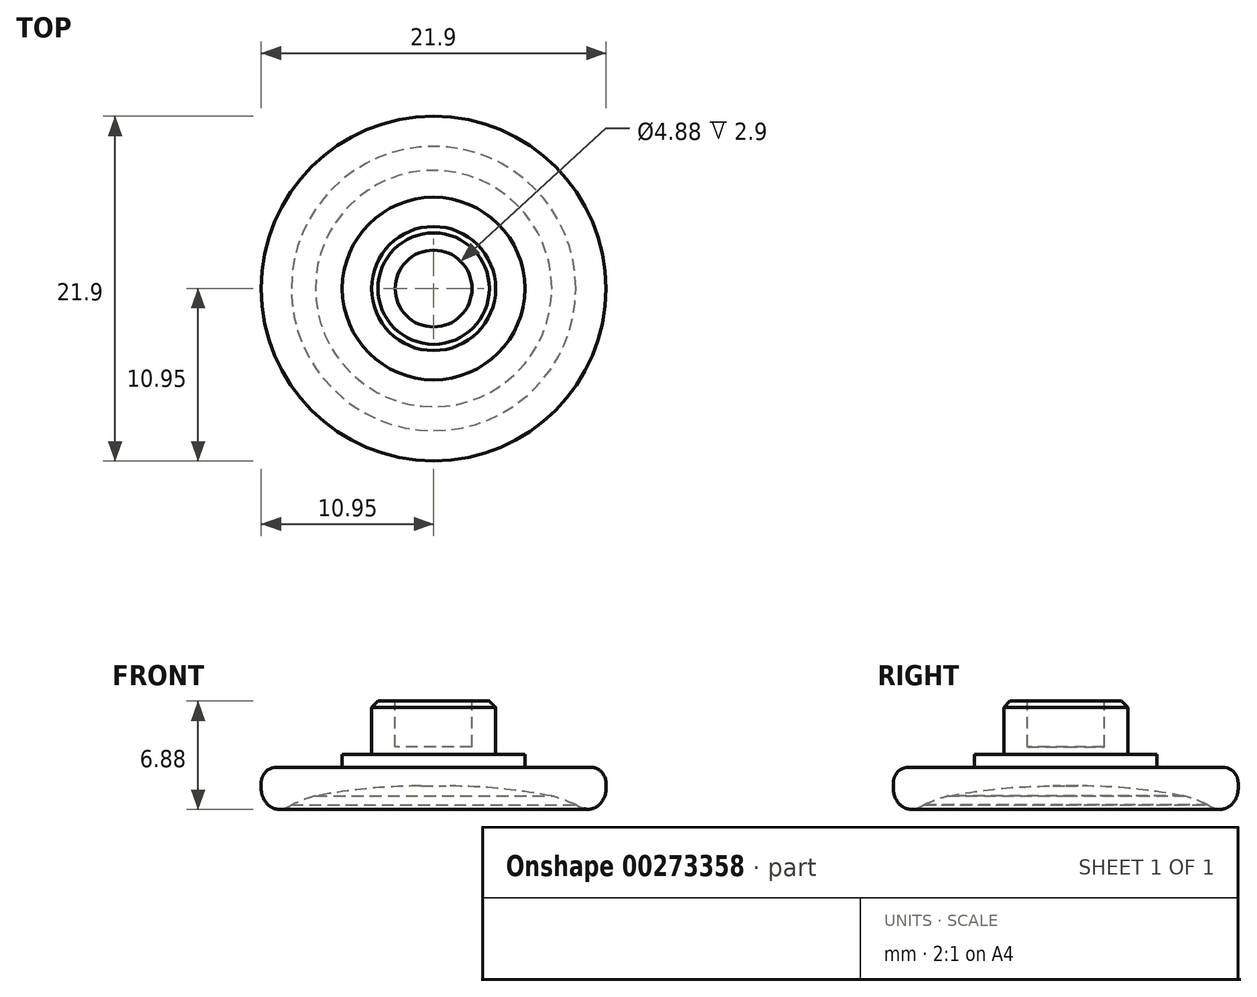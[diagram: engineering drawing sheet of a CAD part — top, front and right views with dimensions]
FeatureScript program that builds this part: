
annotation { "Feature Type Name" : "Feature", "Feature Type Description" : "" }
export const myFeature = defineFeature(function(context is Context, id is Id, definition is map)
    precondition{}
    {
        {
            var Q0;
            Q0=qCreatedBy(makeId("Top.planeOp"),FACE);
            var sketch = newSketch(context, id + "F0", { "sketchPlane" : qUnion([Q0])});
            skCircle(sketch, "E0", {"center": v(0, 0) * mm, "radius": 10.95 * mm});
            skSolve(sketch);
        }
        {
            var Q0;
            Q0=makeQuery(id+"F0.imprint","IMPRINT",FACE,{"disambiguationData":[TD([[makeQuery(id+"F0.imprint","IMPRINT",EDGE,{"derivedFrom":sQuery(id+"F0.wireOp",EDGE,"E0")}),1.0]])]});
            extrude(context, id + "F1", {"entities" : qUnion([Q0]), "depth" : 2.7 * mm});
        }
        {
            var Q0;
            Q0=makeQuery(id+"F1.opExtrude","CAP_FACE",FACE,{"disambiguationData":[OSD([sQuery(id+"F0.wireOp",EDGE,"E0")])],"isStart":false});
            var sketch = newSketch(context, id + "F2", { "sketchPlane" : qUnion([Q0])});
            skCircle(sketch, "E1", {"center": v(0, 0) * mm, "radius": 3.94 * mm});
            skSolve(sketch);
        }
        {
            var Q0;
            Q0=makeQuery(id+"F2.imprint","IMPRINT",FACE,{"disambiguationData":[TD([[makeQuery(id+"F2.imprint","IMPRINT",EDGE,{"derivedFrom":sQuery(id+"F2.wireOp",EDGE,"E1")}),1.0]])]});
            extrude(context, id + "F3", {"entities" : qUnion([Q0]), "operationType" : NewBodyOperationType.ADD, "depth" : 4.2 * mm, "offsetDistance" : 25 * mm});
        }
        {
            var Q0;
            Q0=makeQuery(id+"F1.opExtrude","CAP_EDGE",EDGE,{"disambiguationData":[OSD([sQuery(id+"F0.wireOp",EDGE,"E0")])],"isStart":false});
            fillet(context, id + "F4", {"entities" : qUnion([Q0]), "radius" : 1 * mm, "tangentPropagation" : true, "allowEdgeOverflow" : false});
        }
        {
            var Q0;
            Q0=makeQuery(id+"F1.opExtrude","CAP_FACE",FACE,{"disambiguationData":[OSD([sQuery(id+"F0.wireOp",EDGE,"E0")])],"isStart":false});
            var sketch = newSketch(context, id + "F5", { "sketchPlane" : qUnion([Q0])});
            skCircle(sketch, "E2", {"center": v(0, 0) * mm, "radius": 5.8 * mm});
            skSolve(sketch);
        }
        {
            var Q0;
            Q0=makeQuery(id+"F5.imprint","IMPRINT",FACE,{"disambiguationData":[TD([[makeQuery(id+"F5.imprint","IMPRINT",EDGE,{"derivedFrom":sQuery(id+"F5.wireOp",EDGE,"E2")}),1.0]])]});
            extrude(context, id + "F6", {"entities" : qUnion([Q0]), "operationType" : NewBodyOperationType.ADD, "depth" : .8 * mm, "offsetDistance" : 25 * mm});
        }
        {
            var Q0;
            Q0=makeQuery(id+"F3.opExtrude","CAP_FACE",FACE,{"disambiguationData":[OSD([sQuery(id+"F2.wireOp",EDGE,"E1")])],"isStart":false});
            var sketch = newSketch(context, id + "F7", { "sketchPlane" : qUnion([Q0])});
            skCircle(sketch, "E3", {"center": v(0, 0) * mm, "radius": 2.44 * mm});
            skSolve(sketch);
        }
        {
            var Q0;
            Q0=makeQuery(id+"F7.imprint","IMPRINT",FACE,{"disambiguationData":[TD([[makeQuery(id+"F7.imprint","IMPRINT",EDGE,{"derivedFrom":sQuery(id+"F7.wireOp",EDGE,"E3")}),1.0]])]});
            extrude(context, id + "F8", {"entities" : qUnion([Q0]), "operationType" : NewBodyOperationType.REMOVE, "oppositeDirection" : true, "depth" : 2.9 * mm, "offsetDistance" : 25 * mm});
        }
        {
            var Q0;
            Q0=qCreatedBy(makeId("Right.planeOp"),FACE);
            var sketch = newSketch(context, id + "F9", { "sketchPlane" : qUnion([Q0])});
            skLineSegment(sketch, "E4", {"start": v(0, 0) * mm, "end": v(0, 1.5) * mm});
            skLineSegment(sketch, "E5", {"start": v(0, 1.5) * mm, "end": v(-0.8, 1.5) * mm});
            skLineSegment(sketch, "E6", {"start": v(0, 0) * mm, "end": v(0, -0.4) * mm});
            skLineSegment(sketch, "E7", {"start": v(0, 0) * mm, "end": v(0, -5.92) * mm});
            skLineSegment(sketch, "E8", {"start": v(-11.4, 0) * mm, "end": v(-10, 0) * mm, "construction": true});
            skLineSegment(sketch, "E9", {"start": v(0, -0.4) * mm, "end": v(-10, -0.4) * mm});
            skLineSegment(sketch, "E10", {"start": v(-10, -0.4) * mm, "end": v(-10, 0) * mm});
            skArc(sketch, "E11", {"start": v(-0.8, 1.5) * mm, "mid": v(-4.17, 1.34) * mm, "end": v(-7.5, 0.87) * mm});
            skArc(sketch, "E12", {"start": v(-10, 0) * mm, "mid": v(-9.5, 0.08) * mm, "end": v(-9.03, 0.3) * mm});
            skArc(sketch, "E13", {"start": v(-7.5, 0.87) * mm, "mid": v(-8.28, 0.62) * mm, "end": v(-9.03, 0.3) * mm});
            skSolve(sketch);
        }
        {
            var Q0;
            {var subQ1=sQuery(id+"F9.wireOp",EDGE,"E4");Q0=makeQuery(id+"F9.imprint","IMPRINT",FACE,{"disambiguationData":[TD([[makeQuery(id+"F9.imprint","IMPRINT",EDGE,{"derivedFrom":subQ1}),1.0]])]});}
            var Q1;
            Q1=sQuery(id+"F9.wireOp",EDGE,"E7");
            revolve(context, id + "F10", {"operationType" : NewBodyOperationType.REMOVE, "entities" : qUnion([Q0]), "axis" : qUnion([Q1]), "revolveType" : RevolveType.FULL, "oppositeDirection" : true});
        }
        {
            var Q0;
            Q0=makeQuery(id+"F1.opExtrude","CAP_EDGE",EDGE,{"disambiguationData":[OSD([sQuery(id+"F0.wireOp",EDGE,"E0")])],"isStart":true});
            fillet(context, id + "F11", {"entities" : qUnion([Q0]), "radius" : 1.4 * mm, "tangentPropagation" : true, "allowEdgeOverflow" : false});
        }
        {
            var Q0;
            Q0=makeQuery(id+"F3.opExtrude","CAP_EDGE",EDGE,{"disambiguationData":[OSD([sQuery(id+"F2.wireOp",EDGE,"E1")])],"isStart":false});
            chamfer(context, id + "F12", {"entities" : qUnion([Q0]), "width" : .4 * mm, "tangentPropagation" : true});
        }
        {
            var Q0;
            Q0=makeQuery(id+"F11.opFillet","BLEND_EDGE",EDGE,{"blendedFrom":[makeQuery(id+"F1.opExtrude","CAP_EDGE",EDGE,{"disambiguationData":[OSD([sQuery(id+"F0.wireOp",EDGE,"E0")])],"isStart":true}),makeQuery(id+"F10.boolean.opBoolean","COPY",FACE,{"derivedFrom":makeQuery(id+"F10.opRevolve","SWEPT_FACE",FACE,{"disambiguationData":[OSD([sQuery(id+"F9.wireOp",EDGE,"E12")])]})})],"blendedInto":[makeQuery(id+"F10.boolean.opBoolean","COPY",FACE,{"derivedFrom":makeQuery(id+"F10.opRevolve","SWEPT_FACE",FACE,{"disambiguationData":[OSD([sQuery(id+"F9.wireOp",EDGE,"E12")])]})})]});
            fillet(context, id + "F13", {"entities" : qUnion([Q0]), "radius" : 1 * mm, "tangentPropagation" : true, "allowEdgeOverflow" : false});
        }
    });
